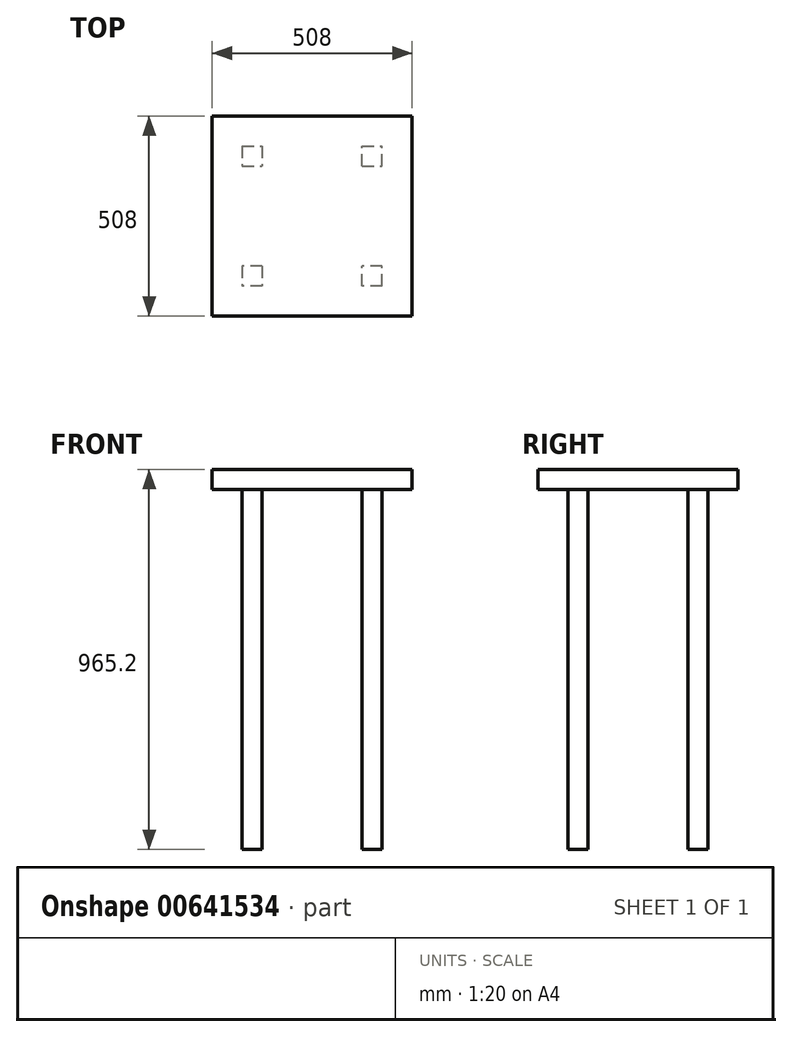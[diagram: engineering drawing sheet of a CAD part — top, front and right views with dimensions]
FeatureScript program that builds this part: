
annotation { "Feature Type Name" : "Feature", "Feature Type Description" : "" }
export const myFeature = defineFeature(function(context is Context, id is Id, definition is map)
    precondition{}
    {
        {
            var Q0;
            Q0=qCreatedBy(makeId("Top.planeOp"),FACE);
            var sketch = newSketch(context, id + "F0", { "sketchPlane" : qUnion([Q0])});
            skLineSegment(sketch, "E0.bottom", {"start": v(254, 254) * mm, "end": v(-254, 254) * mm});
            skLineSegment(sketch, "E0.top", {"start": v(254, -254) * mm, "end": v(-254, -254) * mm});
            skLineSegment(sketch, "E0.left", {"start": v(254, 254) * mm, "end": v(254, -254) * mm});
            skLineSegment(sketch, "E0.right", {"start": v(-254, 254) * mm, "end": v(-254, -254) * mm});
            skPoint(sketch, "E0.middle", {"position": v(0, 0) * mm});
            skSolve(sketch);
        }
        {
            var Q0;
            Q0=makeQuery(id+"F0.imprint","IMPRINT",FACE,{"disambiguationData":[TD([[makeQuery(id+"F0.imprint","IMPRINT",EDGE,{"derivedFrom":sQuery(id+"F0.wireOp",EDGE,"E0.bottom")}),1.0]])]});
            extrude(context, id + "F1", {"entities" : qUnion([Q0]), "depth" : 50.8 * mm, "offsetDistance" : 25.4 * mm});
        }
        {
            var Q0;
            Q0=makeQuery(id+"F1.opExtrude","CAP_FACE",FACE,{"disambiguationData":[OSD([sQuery(id+"F0.wireOp",EDGE,"E0.bottom"),sQuery(id+"F0.wireOp",EDGE,"E0.top"),sQuery(id+"F0.wireOp",EDGE,"E0.left"),sQuery(id+"F0.wireOp",EDGE,"E0.right")])],"isStart":true});
            var sketch = newSketch(context, id + "F2", { "sketchPlane" : qUnion([Q0])});
            skLineSegment(sketch, "E1.bottom", {"start": v(-127, 127) * mm, "end": v(-177.8, 127) * mm});
            skLineSegment(sketch, "E1.top", {"start": v(-127, 177.8) * mm, "end": v(-177.8, 177.8) * mm});
            skLineSegment(sketch, "E1.left", {"start": v(-127, 127) * mm, "end": v(-127, 177.8) * mm});
            skLineSegment(sketch, "E1.right", {"start": v(-177.8, 127) * mm, "end": v(-177.8, 177.8) * mm});
            skPoint(sketch, "E1.middle", {"position": v(-152.4, 152.4) * mm});
            skLineSegment(sketch, "E2.bottom", {"start": v(177.8, 177.8) * mm, "end": v(127, 177.8) * mm});
            skLineSegment(sketch, "E2.top", {"start": v(177.8, 127) * mm, "end": v(127, 127) * mm});
            skLineSegment(sketch, "E2.left", {"start": v(177.8, 177.8) * mm, "end": v(177.8, 127) * mm});
            skLineSegment(sketch, "E2.right", {"start": v(127, 177.8) * mm, "end": v(127, 127) * mm});
            skPoint(sketch, "E2.middle", {"position": v(152.4, 152.4) * mm});
            skLineSegment(sketch, "E3.bottom", {"start": v(-177.8, -177.8) * mm, "end": v(-127, -177.8) * mm});
            skLineSegment(sketch, "E3.top", {"start": v(-177.8, -127) * mm, "end": v(-127, -127) * mm});
            skLineSegment(sketch, "E3.left", {"start": v(-177.8, -177.8) * mm, "end": v(-177.8, -127) * mm});
            skLineSegment(sketch, "E3.right", {"start": v(-127, -177.8) * mm, "end": v(-127, -127) * mm});
            skPoint(sketch, "E3.middle", {"position": v(-152.4, -152.4) * mm});
            skLineSegment(sketch, "E4.bottom", {"start": v(127, -127) * mm, "end": v(177.8, -127) * mm});
            skLineSegment(sketch, "E4.top", {"start": v(127, -177.8) * mm, "end": v(177.8, -177.8) * mm});
            skLineSegment(sketch, "E4.left", {"start": v(127, -127) * mm, "end": v(127, -177.8) * mm});
            skLineSegment(sketch, "E4.right", {"start": v(177.8, -127) * mm, "end": v(177.8, -177.8) * mm});
            skPoint(sketch, "E4.middle", {"position": v(152.4, -152.4) * mm});
            skSolve(sketch);
        }
        {
            var Q0;
            Q0=makeQuery(id+"F2.imprint","IMPRINT",FACE,{"disambiguationData":[TD([[makeQuery(id+"F2.imprint","IMPRINT",EDGE,{"derivedFrom":sQuery(id+"F2.wireOp",EDGE,"E1.bottom")}),-1.0]])]});
            var Q1;
            Q1=makeQuery(id+"F2.imprint","IMPRINT",FACE,{"disambiguationData":[TD([[makeQuery(id+"F2.imprint","IMPRINT",EDGE,{"derivedFrom":sQuery(id+"F2.wireOp",EDGE,"E2.bottom")}),1.0]])]});
            var Q2;
            Q2=makeQuery(id+"F2.imprint","IMPRINT",FACE,{"disambiguationData":[TD([[makeQuery(id+"F2.imprint","IMPRINT",EDGE,{"derivedFrom":sQuery(id+"F2.wireOp",EDGE,"E4.bottom")}),-1.0]])]});
            var Q3;
            Q3=makeQuery(id+"F2.imprint","IMPRINT",FACE,{"disambiguationData":[TD([[makeQuery(id+"F2.imprint","IMPRINT",EDGE,{"derivedFrom":sQuery(id+"F2.wireOp",EDGE,"E3.bottom")}),1.0]])]});
            extrude(context, id + "F3", {"entities" : qUnion([Q0, Q1, Q2, Q3]), "operationType" : NewBodyOperationType.ADD, "depth" : 914.4 * mm, "offsetDistance" : 25.4 * mm});
        }
    });
